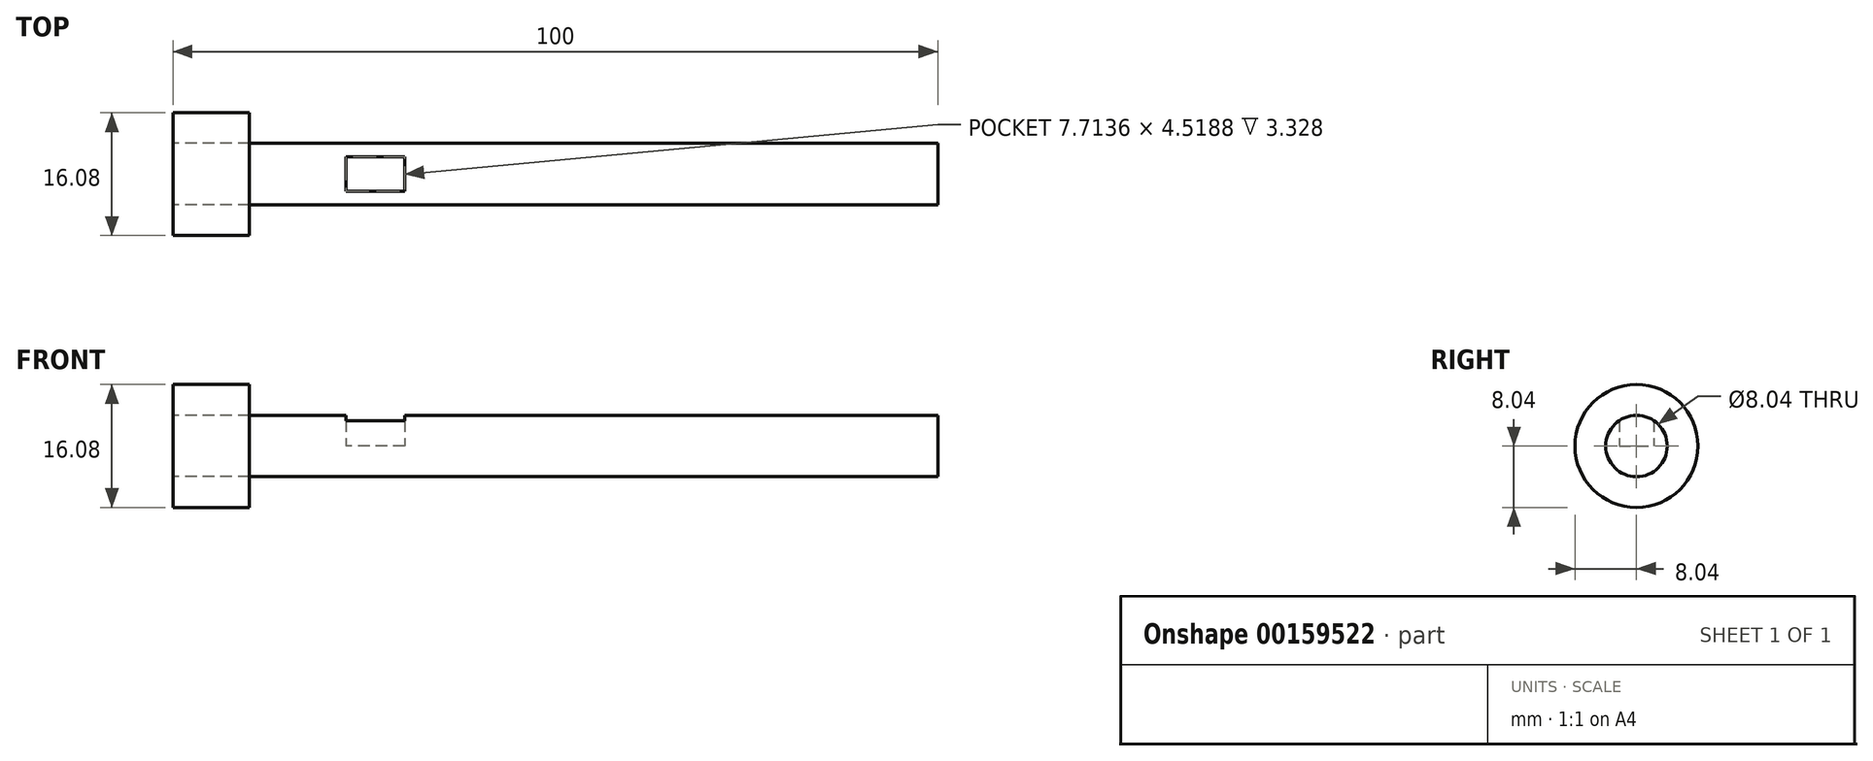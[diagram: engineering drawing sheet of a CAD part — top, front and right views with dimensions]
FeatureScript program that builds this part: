
annotation { "Feature Type Name" : "Feature", "Feature Type Description" : "" }
export const myFeature = defineFeature(function(context is Context, id is Id, definition is map)
    precondition{}
    {
        {
            var Q0;
            Q0=qCreatedBy(makeId("Top.planeOp"),FACE);
            var sketch = newSketch(context, id + "F0", { "sketchPlane" : qUnion([Q0])});
            skLineSegment(sketch, "E0.bottom", {"start": v(-22.6, 8.04) * mm, "end": v(-12.6, 8.04) * mm});
            skLineSegment(sketch, "E0.top", {"start": v(-22.6, 0) * mm, "end": v(-12.6, 0) * mm});
            skLineSegment(sketch, "E0.left", {"start": v(-22.6, 8.04) * mm, "end": v(-22.6, 0) * mm});
            skLineSegment(sketch, "E0.right", {"start": v(-12.6, 8.04) * mm, "end": v(-12.6, 0) * mm});
            skLineSegment(sketch, "E1.bottom", {"start": v(-22.6, 4.02) * mm, "end": v(77.4, 4.02) * mm});
            skLineSegment(sketch, "E1.top", {"start": v(-22.6, 0) * mm, "end": v(77.4, 0) * mm});
            skLineSegment(sketch, "E1.left", {"start": v(-22.6, 4.02) * mm, "end": v(-22.6, 0) * mm});
            skLineSegment(sketch, "E1.right", {"start": v(77.4, 4.02) * mm, "end": v(77.4, 0) * mm});
            skLineSegment(sketch, "E2", {"start": v(-42.65, 0) * mm, "end": v(71.9, 0) * mm, "construction": true});
            skSolve(sketch);
        }
        {
            var Q0;
            {var subQ0=sQuery(id+"F0.wireOp",EDGE,"E0.bottom");Q0=makeQuery(id+"F0.imprint","IMPRINT",FACE,{"disambiguationData":[TD([[makeQuery(id+"F0.imprint","IMPRINT",EDGE,{"derivedFrom":subQ0}),-1.0]])]});}
            var Q1;
            {var subQ5=sQuery(id+"F0.wireOp",EDGE,"E1.left");Q1=makeQuery(id+"F0.imprint","IMPRINT",FACE,{"disambiguationData":[TD([[makeQuery(id+"F0.imprint","IMPRINT",EDGE,{"derivedFrom":subQ5}),1.0]])]});}
            var Q2;
            {var subQ5=sQuery(id+"F0.wireOp",EDGE,"E1.right");Q2=makeQuery(id+"F0.imprint","IMPRINT",FACE,{"disambiguationData":[TD([[makeQuery(id+"F0.imprint","IMPRINT",EDGE,{"derivedFrom":subQ5}),-1.0]])]});}
            var Q3;
            Q3=sQuery(id+"F0.wireOp",EDGE,"E0.right");
            var Q4;
            Q4=sQuery(id+"F0.wireOp",EDGE,"E1.bottom");
            var Q5;
            Q5=sQuery(id+"F0.wireOp",EDGE,"E1.top");
            var Q6;
            Q6=sQuery(id+"F0.wireOp",EDGE,"E0.top");
            var Q7;
            Q7=sQuery(id+"F0.wireOp",EDGE,"E0.bottom");
            var Q8;
            Q8=sQuery(id+"F0.wireOp",EDGE,"E1.right");
            var Q9;
            Q9=sQuery(id+"F0.wireOp",EDGE,"E0.left");
            var Q10;
            Q10=sQuery(id+"F0.wireOp",EDGE,"E1.left");
            var Q11;
            Q11=sQuery(id+"F0.wireOp",EDGE,"E2");
            revolve(context, id + "F1", {"entities" : qUnion([Q0, Q1, Q2]), "surfaceEntities" : qUnion([Q3, Q4, Q5, Q6, Q7, Q8, Q9, Q10]), "axis" : qUnion([Q11]), "revolveType" : RevolveType.FULL});
        }
        {
            var Q0;
            Q0=qCreatedBy(makeId("Top.planeOp"),FACE);
            var sketch = newSketch(context, id + "F2", { "sketchPlane" : qUnion([Q0])});
            skLineSegment(sketch, "E3.bottom", {"start": v(7.71, -2.26) * mm, "end": v(0, -2.26) * mm});
            skLineSegment(sketch, "E3.top", {"start": v(7.71, 2.26) * mm, "end": v(0, 2.26) * mm});
            skLineSegment(sketch, "E3.left", {"start": v(7.71, -2.26) * mm, "end": v(7.71, 2.26) * mm});
            skLineSegment(sketch, "E3.right", {"start": v(0, -2.26) * mm, "end": v(0, 2.26) * mm});
            skSolve(sketch);
        }
        {
            var Q0;
            Q0=makeQuery(id+"F2.imprint","IMPRINT",FACE,{"disambiguationData":[TD([[makeQuery(id+"F2.imprint","IMPRINT",EDGE,{"derivedFrom":sQuery(id+"F2.wireOp",EDGE,"E3.bottom")}),-1.0]])]});
            var Q1;
            Q1=sQuery(id+"F2.wireOp",EDGE,"E3.right");
            var Q2;
            Q2=sQuery(id+"F2.wireOp",EDGE,"E3.left");
            var Q3;
            Q3=sQuery(id+"F2.wireOp",EDGE,"E3.top");
            var Q4;
            Q4=sQuery(id+"F2.wireOp",EDGE,"E3.bottom");
            extrude(context, id + "F3", {"entities" : qUnion([Q0]), "operationType" : NewBodyOperationType.REMOVE, "surfaceEntities" : qUnion([Q1, Q2, Q3, Q4]), "depth" : 10 * mm});
        }
    });
